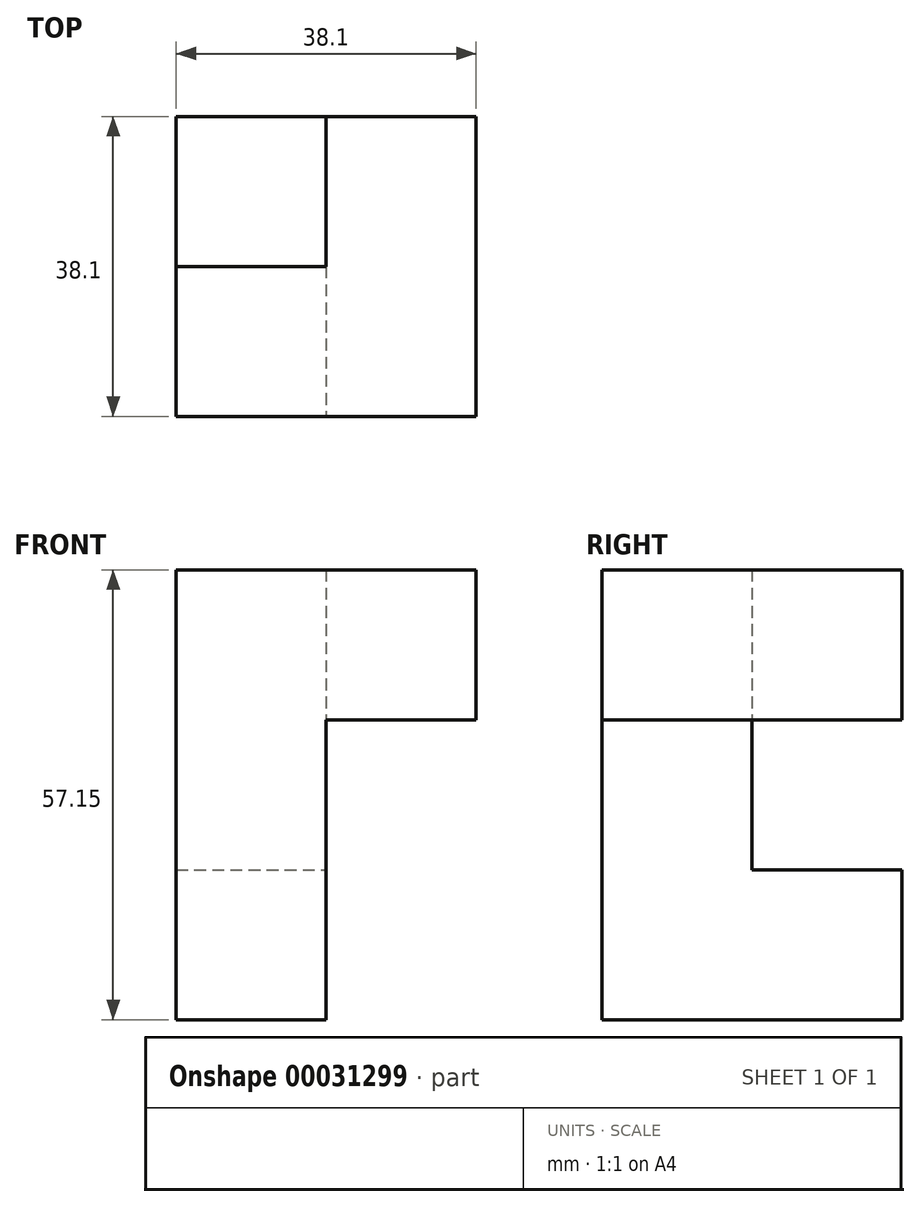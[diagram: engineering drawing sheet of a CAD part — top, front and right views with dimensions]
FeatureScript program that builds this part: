
annotation { "Feature Type Name" : "Feature", "Feature Type Description" : "" }
export const myFeature = defineFeature(function(context is Context, id is Id, definition is map)
    precondition{}
    {
        {
            var Q0;
            Q0=qCreatedBy(makeId("Top.planeOp"),FACE);
            var sketch = newSketch(context, id + "F0", { "sketchPlane" : qUnion([Q0])});
            skLineSegment(sketch, "E0", {"start": v(-4.98, 38.1) * mm, "end": v(14.07, 38.1) * mm});
            skLineSegment(sketch, "E1", {"start": v(14.07, 38.1) * mm, "end": v(14.07, 0) * mm});
            skLineSegment(sketch, "E2", {"start": v(-4.98, 38.1) * mm, "end": v(-4.98, 19.05) * mm});
            skLineSegment(sketch, "E3", {"start": v(-4.98, 19.05) * mm, "end": v(-24.03, 19.05) * mm});
            skLineSegment(sketch, "E4", {"start": v(-24.03, 19.05) * mm, "end": v(-24.03, 0) * mm});
            skLineSegment(sketch, "E5", {"start": v(-24.03, 0) * mm, "end": v(14.07, 0) * mm});
            skSolve(sketch);
        }
        {
            var Q0;
            Q0=makeQuery(id+"F0.imprint","IMPRINT",FACE,{"disambiguationData":[TD([[makeQuery(id+"F0.imprint","IMPRINT",EDGE,{"derivedFrom":sQuery(id+"F0.wireOp",EDGE,"E0")}),-1.0]])]});
            extrude(context, id + "F1", {"entities" : qUnion([Q0]), "depth" : 19.05 * mm});
        }
        {
            var Q0;
            Q0=makeQuery(id+"F1.opExtrude","CAP_FACE",FACE,{"disambiguationData":[OSD([sQuery(id+"F0.wireOp",EDGE,"E0"),sQuery(id+"F0.wireOp",EDGE,"E1"),sQuery(id+"F0.wireOp",EDGE,"E2"),sQuery(id+"F0.wireOp",EDGE,"E3"),sQuery(id+"F0.wireOp",EDGE,"E4"),sQuery(id+"F0.wireOp",EDGE,"E5")])],"isStart":true});
            var sketch = newSketch(context, id + "F2", { "sketchPlane" : qUnion([Q0])});
            skLineSegment(sketch, "E6", {"start": v(-24.03, 0) * mm, "end": v(-24.03, -19.05) * mm});
            skLineSegment(sketch, "E7", {"start": v(-24.03, -19.05) * mm, "end": v(-4.98, -19.05) * mm});
            skLineSegment(sketch, "E8", {"start": v(-4.98, -19.05) * mm, "end": v(-4.98, 0) * mm});
            skLineSegment(sketch, "E9", {"start": v(-4.98, 0) * mm, "end": v(-24.03, 0) * mm});
            skSolve(sketch);
        }
        {
            var Q0;
            Q0=makeQuery(id+"F2.imprint","IMPRINT",FACE,{"disambiguationData":[TD([[makeQuery(id+"F2.imprint","IMPRINT",EDGE,{"derivedFrom":sQuery(id+"F2.wireOp",EDGE,"E6")}),-1.0]])]});
            extrude(context, id + "F3", {"entities" : qUnion([Q0]), "operationType" : NewBodyOperationType.ADD, "depth" : 38.1 * mm});
        }
        {
            var Q0;
            Q0=makeQuery(id+"F3.boolean.opBoolean","MERGE",FACE,{"derivedFrom":[makeQuery(id+"F1.opExtrude","SWEPT_FACE",FACE,{"disambiguationData":[OSD([sQuery(id+"F0.wireOp",EDGE,"E3")])]}),makeQuery(id+"F3.opExtrude","SWEPT_FACE",FACE,{"disambiguationData":[OSD([sQuery(id+"F2.wireOp",EDGE,"E7")])]})]});
            var sketch = newSketch(context, id + "F4", { "sketchPlane" : qUnion([Q0])});
            skLineSegment(sketch, "E10", {"start": v(24.03, -38.1) * mm, "end": v(24.03, -19.05) * mm});
            skLineSegment(sketch, "E11", {"start": v(24.03, -19.05) * mm, "end": v(4.98, -19.05) * mm});
            skLineSegment(sketch, "E12", {"start": v(4.98, -19.05) * mm, "end": v(4.98, -38.1) * mm});
            skLineSegment(sketch, "E13", {"start": v(4.98, -38.1) * mm, "end": v(24.03, -38.1) * mm});
            skSolve(sketch);
        }
        {
            var Q0;
            Q0=makeQuery(id+"F4.imprint","IMPRINT",FACE,{"disambiguationData":[TD([[makeQuery(id+"F4.imprint","IMPRINT",EDGE,{"derivedFrom":sQuery(id+"F4.wireOp",EDGE,"E10")}),-1.0]])]});
            extrude(context, id + "F5", {"entities" : qUnion([Q0]), "operationType" : NewBodyOperationType.ADD, "depth" : 19.05 * mm});
        }
    });
